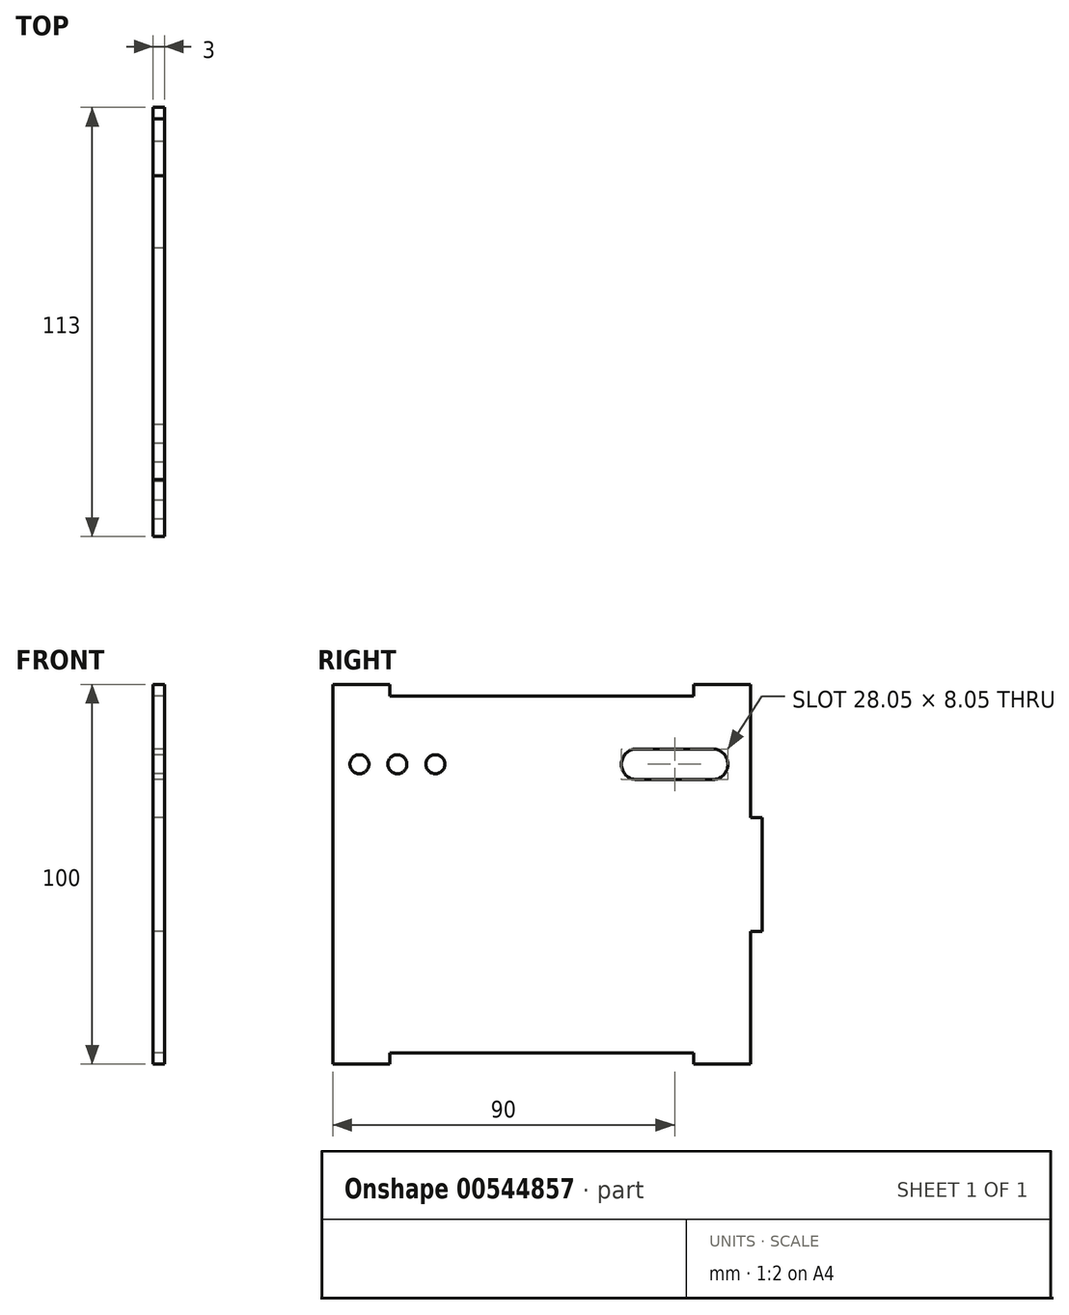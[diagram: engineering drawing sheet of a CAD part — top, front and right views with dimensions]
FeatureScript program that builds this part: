
annotation { "Feature Type Name" : "Feature", "Feature Type Description" : "" }
export const myFeature = defineFeature(function(context is Context, id is Id, definition is map)
    precondition{}
    {
        {
            var Q0;
            Q0=qCreatedBy(makeId("Right.planeOp"),FACE);
            var sketch = newSketch(context, id + "F0", { "sketchPlane" : qUnion([Q0])});
            skLineSegment(sketch, "E0.bottom", {"start": v(30, 21) * mm, "end": v(30, -14) * mm});
            skLineSegment(sketch, "E0.top", {"start": v(-80, 21) * mm, "end": v(-80, -79) * mm});
            skLineSegment(sketch, "E0.left", {"start": v(30, 21) * mm, "end": v(15, 21) * mm});
            skLineSegment(sketch, "E0.right", {"start": v(30, -79) * mm, "end": v(15, -79) * mm});
            skLineSegment(sketch, "E1.bottom", {"start": v(15, 21) * mm, "end": v(15, 18) * mm});
            skLineSegment(sketch, "E1.right", {"start": v(15, 18) * mm, "end": v(-65, 18) * mm});
            skLineSegment(sketch, "E2", {"start": v(-65, -76) * mm, "end": v(15, -76) * mm});
            skLineSegment(sketch, "E3", {"start": v(15, -76) * mm, "end": v(15, -79) * mm});
            skLineSegment(sketch, "E4", {"start": v(-65, -76) * mm, "end": v(-65, -79) * mm});
            skLineSegment(sketch, "E5", {"start": v(-65, -79) * mm, "end": v(-80, -79) * mm});
            skLineSegment(sketch, "E6", {"start": v(-65, 18) * mm, "end": v(-65, 21) * mm});
            skLineSegment(sketch, "E7", {"start": v(-65, 21) * mm, "end": v(-80, 21) * mm});
            skLineSegment(sketch, "E8", {"start": v(33, -29) * mm, "end": v(-80, -29) * mm, "construction": true});
            skLineSegment(sketch, "E9.left", {"start": v(20, 4.03) * mm, "end": v(0, 4.03) * mm});
            skLineSegment(sketch, "E9.right", {"start": v(20, -4.03) * mm, "end": v(0, -4.02) * mm});
            skLineSegment(sketch, "E10", {"start": v(0, 0) * mm, "end": v(20, 0) * mm, "construction": true});
            skArc(sketch, "E11", {"start": v(0, 4.02) * mm, "mid": v(-4.02, 0) * mm, "end": v(0, -4.02) * mm});
            skCircle(sketch, "E12", {"center": v(0, 0) * mm, "radius": 14 * mm, "construction": true});
            skPoint(sketch, "E13.orphan", {"position": v(-15.84, 0) * mm});
            skLineSegment(sketch, "E14", {"start": v(-53, 0) * mm, "end": v(-73, 0) * mm, "construction": true});
            skPoint(sketch, "E14.endSnap0", {"position": v(-4.02, 0) * mm});
            skCircle(sketch, "E15", {"center": v(-53, 0) * mm, "radius": 2.5 * mm});
            skCircle(sketch, "E16", {"center": v(-63, 0) * mm, "radius": 2.5 * mm});
            skCircle(sketch, "E17", {"center": v(-73, 0) * mm, "radius": 2.5 * mm});
            skLineSegment(sketch, "E18.bottom", {"start": v(30, -14) * mm, "end": v(33, -14) * mm});
            skLineSegment(sketch, "E18.top", {"start": v(30, -44) * mm, "end": v(33, -44) * mm});
            skLineSegment(sketch, "E18.right", {"start": v(33, -14) * mm, "end": v(33, -44) * mm});
            skLineSegment(sketch, "E19.trimOffspring", {"start": v(30, -44) * mm, "end": v(30, -79) * mm});
            skPoint(sketch, "E20.orphan", {"position": v(30, -29) * mm});
            skArc(sketch, "E21", {"start": v(20, -4.02) * mm, "mid": v(24.02, 0) * mm, "end": v(20, 4.03) * mm});
            skSolve(sketch);
        }
        {
            var Q0;
            Q0 = qSketchRegion(id + "F0", true);
            extrude(context, id + "F1", {"entities" : qUnion([Q0]), "depth" : 3 * mm, "offsetDistance" : 25 * mm});
        }
    });
